# Revit family: AISC WT Shapes-Section
name_source: partatom
category: Detail Items
revit_build: Autodesk Revit Architecture 2012 (Build: 20110210_1515)
units: mm (PartAtom-declared; Revit-internal decimal feet)

## types (275) — shared parameters
Keynote = 05 12 00.N0
y = 0' - 2 31/32"

## per-type parameters (varying)
| type | A | W | bf | d | k | r | tf | tw |
| WT22X167.5 | 0.34 SF | 168 | 1' - 3 29/32" | 1' - 10" | 0' - 2 5/8" | 0' - 0 27/32" | 0' - 1 25/32" | 0' - 1 1/32" |
| WT22X145 | 0.3 SF | 145 | 1' - 3 13/16" | 1' - 9 13/16" | 0' - 2 7/16" | 0' - 0 27/32" | 0' - 1 19/32" | 0' - 0 7/8" |
| WT22X131 | 0.27 SF | 131 | 1' - 3 13/16" | 1' - 9 11/16" | 0' - 2 1/4" | 0' - 0 27/32" | 0' - 1 13/32" | 0' - 0 25/32" |
| WT22X115 | 0.23 SF | 115 | 1' - 3 13/16" | 1' - 9 1/2" | 0' - 2 1/16" | 0' - 0 27/32" | 0' - 1 7/32" | 0' - 0 23/32" |
| WT20X296.5 | 0.61 SF | 296 | 1' - 4 11/16" | 1' - 9 1/2" | 0' - 4 1/2" | 0' - 1 9/32" | 0' - 3 7/32" | 0' - 1 25/32" |
| WT20X251.5 | 0.51 SF | 252 | 1' - 4 13/32" | 1' - 9" | 0' - 4" | 0' - 1 1/4" | 0' - 2 3/4" | 0' - 1 17/32" |
| WT20X215.5 | 0.44 SF | 215 | 1' - 4 3/16" | 1' - 8 19/32" | 0' - 3 5/8" | 0' - 1 1/4" | 0' - 2 3/8" | 0' - 1 11/32" |
| WT20X198.5 | 0.41 SF | 198 | 1' - 4 3/32" | 1' - 8 1/2" | 0' - 3 1/2" | 0' - 1 5/16" | 0' - 2 3/16" | 0' - 1 7/32" |
| WT20X186 | 0.38 SF | 186 | 1' - 4 3/32" | 1' - 8 5/16" | 0' - 3 5/16" | 0' - 1 1/4" | 0' - 2 1/16" | 0' - 1 5/32" |
| WT20X181 | 0.37 SF | 181 | 1' - 4" | 1' - 8 5/16" | 0' - 3 1/4" | 0' - 1 1/4" | 0' - 2" | 0' - 1 1/8" |
| WT20X162 | 0.33 SF | 162 | 1' - 3 29/32" | 1' - 8 3/32" | 0' - 3 1/16" | 0' - 1 1/4" | 0' - 1 13/16" | 0' - 1" |
| WT20X148.5 | 0.3 SF | 148 | 1' - 3 13/16" | 1' - 7 29/32" | 0' - 2 15/16" | 0' - 1 9/32" | 0' - 1 21/32" | 0' - 0 15/16" |
| WT20X138.5 | 0.28 SF | 138 | 1' - 3 13/16" | 1' - 7 13/16" | 0' - 2 7/8" | 0' - 1 9/32" | 0' - 1 19/32" | 0' - 0 27/32" |
| WT20X124.5 | 0.25 SF | 125 | 1' - 3 13/16" | 1' - 7 11/16" | 0' - 2 11/16" | 0' - 1 9/32" | 0' - 1 13/32" | 0' - 0 3/4" |
| WT20X107.5 | 0.22 SF | 108 | 1' - 3 13/16" | 1' - 7 1/2" | 0' - 2 1/2" | 0' - 1 9/32" | 0' - 1 7/32" | 0' - 0 21/32" |
| WT20X99.5 | 0.2 SF | 100 | 1' - 3 13/16" | 1' - 7 5/16" | 0' - 2 5/16" | 0' - 1 1/4" | 0' - 1 1/16" | 0' - 0 21/32" |
| WT20X196 | 0.4 SF | 196 | 1' - 0 13/32" | 1' - 8 13/16" | 0' - 3 13/16" | 0' - 1 9/32" | 0' - 2 17/32" | 0' - 1 13/32" |
| WT20X165.5 | 0.34 SF | 166 | 1' - 0 3/16" | 1' - 8 13/32" | 0' - 3 3/8" | 0' - 1 1/4" | 0' - 2 1/8" | 0' - 1 7/32" |
| WT20X163.5 | 0.33 SF | 164 | 1' - 0 3/32" | 1' - 8 13/32" | 0' - 3 3/8" | 0' - 1 1/4" | 0' - 2 1/8" | 0' - 1 3/16" |
| WT20X147 | 0.3 SF | 147 | 1' - 0" | 1' - 8 3/16" | 0' - 3 3/16" | 0' - 1 1/4" | 0' - 1 15/16" | 0' - 1 1/16" |
| WT20X139 | 0.28 SF | 139 | 1' - 0" | 1' - 8 3/32" | 0' - 3 1/16" | 0' - 1 1/4" | 0' - 1 13/16" | 0' - 1 1/32" |
| WT20X132 | 0.27 SF | 132 | 0' - 11 29/32" | 1' - 8" | 0' - 3" | 0' - 1 9/32" | 0' - 1 23/32" | 0' - 0 31/32" |
| WT20X117.5 | 0.24 SF | 118 | 0' - 11 29/32" | 1' - 7 13/16" | 0' - 2 7/8" | 0' - 1 9/32" | 0' - 1 19/32" | 0' - 0 27/32" |
| WT20X105.5 | 0.22 SF | 106 | 0' - 11 13/16" | 1' - 7 11/16" | 0' - 2 11/16" | 0' - 1 9/32" | 0' - 1 13/32" | 0' - 0 3/4" |
| WT20X91.5 | 0.19 SF | 91.5 | 0' - 11 13/16" | 1' - 7 1/2" | 0' - 2 1/2" | 0' - 1 5/16" | 0' - 1 3/16" | 0' - 0 21/32" |
| WT20X83.5 | 0.17 SF | 83.5 | 0' - 11 13/16" | 1' - 7 5/16" | 0' - 2 5/16" | 0' - 1 9/32" | 0' - 1 1/32" | 0' - 0 21/32" |
| WT20X74.5 | 0.15 SF | 74.5 | 0' - 11 13/16" | 1' - 7 3/32" | 0' - 2 1/8" | 0' - 1 9/32" | 0' - 0 27/32" | 0' - 0 5/8" |
| WT18X400 | 0.82 SF | 400 | 1' - 6" | 1' - 9" | 0' - 5 9/16" | 0' - 1 9/32" | 0' - 4 9/32" | 0' - 2 3/8" |
| WT18X326 | 0.67 SF | 325 | 1' - 5 19/32" | 1' - 8 3/16" | 0' - 4 13/16" | 0' - 1 9/32" | 0' - 3 17/32" | 0' - 1 31/32" |
| WT18X264.5 | 0.54 SF | 264 | 1' - 5 3/16" | 1' - 7 19/32" | 0' - 4 3/16" | 0' - 1 9/32" | 0' - 2 29/32" | 0' - 1 5/8" |
| WT18X243.5 | 0.5 SF | 244 | 1' - 5 3/32" | 1' - 7 11/16" | 0' - 4" | 0' - 1 5/16" | 0' - 2 11/16" | 0' - 1 1/2" |
| WT18X220.5 | 0.45 SF | 220 | 1' - 5" | 1' - 7 3/32" | 0' - 3 11/16" | 0' - 1 1/4" | 0' - 2 7/16" | 0' - 1 3/8" |
| WT18X197.5 | 0.4 SF | 198 | 1' - 4 13/16" | 1' - 6 29/32" | 0' - 3 7/16" | 0' - 1 1/4" | 0' - 2 3/16" | 0' - 1 7/32" |
| WT18X180.5 | 0.37 SF | 180 | 1' - 4 11/16" | 1' - 6 11/16" | 0' - 3 1/4" | 0' - 1 1/4" | 0' - 2" | 0' - 1 1/8" |
| WT18X165 | 0.34 SF | 165 | 1' - 4 19/32" | 1' - 6 1/2" | 0' - 3 1/8" | 0' - 1 9/32" | 0' - 1 27/32" | 0' - 1 1/32" |
| WT18X151 | 0.31 SF | 151 | 1' - 4 11/16" | 1' - 6 13/32" | 0' - 2 15/16" | 0' - 1 1/4" | 0' - 1 11/16" | 0' - 0 15/16" |
| WT18X141 | 0.29 SF | 141 | 1' - 4 19/32" | 1' - 6 5/16" | 0' - 2 13/16" | 0' - 1 1/4" | 0' - 1 9/16" | 0' - 0 7/8" |
| WT18X131 | 0.27 SF | 131 | 1' - 4 19/32" | 1' - 6 3/32" | 0' - 2 11/16" | 0' - 1 1/4" | 0' - 1 7/16" | 0' - 0 27/32" |
| WT18X123.5 | 0.25 SF | 124 | 1' - 4 1/2" | 1' - 6" | 0' - 2 5/8" | 0' - 1 9/32" | 0' - 1 11/32" | 0' - 0 13/16" |
| WT18X116 | 0.24 SF | 116 | 1' - 0 3/32" | 1' - 6 19/32" | 0' - 2 7/16" | 0' - 0 7/8" | 0' - 1 9/16" | 0' - 0 7/8" |
| WT18X128 | 0.26 SF | 128 | 1' - 0 3/16" | 1' - 6 11/16" | 0' - 2 5/8" | 0' - 0 29/32" | 0' - 1 23/32" | 0' - 0 31/32" |
| WT18X115.5 | 0.24 SF | 116 | 1' - 0 3/32" | 1' - 6 19/32" | 0' - 2 7/16" | 0' - 0 7/8" | 0' - 1 9/16" | 0' - 0 7/8" |
| WT18X105 | 0.21 SF | 105 | 1' - 0 3/16" | 1' - 6 5/16" | 0' - 2 5/16" | 0' - 0 15/16" | 0' - 1 3/8" | 0' - 0 27/32" |
| WT18X97 | 0.2 SF | 97 | 1' - 0 3/32" | 1' - 6 3/16" | 0' - 2 3/16" | 0' - 0 15/16" | 0' - 1 1/4" | 0' - 0 3/4" |
| WT18X91 | 0.19 SF | 91 | 1' - 0 3/32" | 1' - 6 3/16" | 0' - 2 1/8" | 0' - 0 15/16" | 0' - 1 3/16" | 0' - 0 23/32" |
| WT18X85 | 0.17 SF | 85 | 1' - 0" | 1' - 6 3/32" | 0' - 2" | 0' - 0 29/32" | 0' - 1 3/32" | 0' - 0 11/16" |
| WT18X80 | 0.16 SF | 80 | 1' - 0" | 1' - 6" | 0' - 1 15/16" | 0' - 0 29/32" | 0' - 1 1/32" | 0' - 0 21/32" |
| WT18X75 | 0.15 SF | 75 | 1' - 0" | 1' - 5 29/32" | 0' - 1 7/8" | 0' - 0 15/16" | 0' - 0 15/16" | 0' - 0 5/8" |
| WT18X67.5 | 0.14 SF | 67.5 | 1' - 0" | 1' - 5 13/16" | 0' - 1 11/16" | 0' - 0 29/32" | 0' - 0 25/32" | 0' - 0 19/32" |
| WT16.5X193.5 | 0.4 SF | 194 | 1' - 4 3/16" | 1' - 6" | 0' - 3 3/16" | 0' - 0 29/32" | 0' - 2 9/32" | 0' - 1 1/4" |
| WT16.5X177 | 0.36 SF | 177 | 1' - 4 3/32" | 1' - 5 13/16" | 0' - 2 15/16" | 0' - 0 27/32" | 0' - 2 3/32" | 0' - 1 5/32" |
| WT16.5X159 | 0.33 SF | 159 | 1' - 4" | 1' - 5 19/32" | 0' - 2 3/4" | 0' - 0 7/8" | 0' - 1 7/8" | 0' - 1 1/32" |
| WT16.5X145.5 | 0.3 SF | 146 | 1' - 3 29/32" | 1' - 5 13/32" | 0' - 2 5/8" | 0' - 0 29/32" | 0' - 1 23/32" | 0' - 0 31/32" |
| WT16.5X131.5 | 0.27 SF | 132 | 1' - 3 13/16" | 1' - 5 5/16" | 0' - 2 7/16" | 0' - 0 7/8" | 0' - 1 9/16" | 0' - 0 7/8" |
| WT16.5X120.5 | 0.25 SF | 120 | 1' - 3 29/32" | 1' - 5 3/32" | 0' - 2 1/4" | 0' - 0 27/32" | 0' - 1 13/32" | 0' - 0 27/32" |
| WT16.5X110.5 | 0.23 SF | 110 | 1' - 3 13/16" | 1' - 5" | 0' - 2 1/8" | 0' - 0 27/32" | 0' - 1 9/32" | 0' - 0 25/32" |
| WT16.5X100.5 | 0.21 SF | 100 | 1' - 3 11/16" | 1' - 4 13/16" | 0' - 2" | 0' - 0 27/32" | 0' - 1 5/32" | 0' - 0 23/32" |
| WT16.5X84.5 | 0.17 SF | 84.5 | 0' - 11 1/2" | 1' - 4 29/32" | 0' - 2 1/8" | 0' - 0 29/32" | 0' - 1 7/32" | 0' - 0 21/32" |
| WT16.5X76 | 0.16 SF | 76 | 0' - 11 19/32" | 1' - 4 11/16" | 0' - 1 15/16" | 0' - 0 7/8" | 0' - 1 1/16" | 0' - 0 5/8" |
| WT16.5X70.5 | 0.14 SF | 70.5 | 0' - 11 1/2" | 1' - 4 11/16" | 0' - 1 13/16" | 0' - 0 27/32" | 0' - 0 31/32" | 0' - 0 19/32" |
| WT16.5X65 | 0.13 SF | 65 | 0' - 11 1/2" | 1' - 4 1/2" | 0' - 1 3/4" | 0' - 0 29/32" | 0' - 0 27/32" | 0' - 0 19/32" |
| WT16.5X59 | 0.12 SF | 59 | 0' - 11 1/2" | 1' - 4 13/32" | 0' - 1 5/8" | 0' - 0 7/8" | 0' - 0 3/4" | 0' - 0 9/16" |
| WT15X195.5 | 0.4 SF | 196 | 1' - 3 19/32" | 1' - 4 19/32" | 0' - 3 3/8" | 0' - 0 15/16" | 0' - 2 7/16" | 0' - 1 3/8" |
| WT15X178.5 | 0.36 SF | 178 | 1' - 3 1/2" | 1' - 4 13/32" | 0' - 3 1/8" | 0' - 0 7/8" | 0' - 2 1/4" | 0' - 1 1/4" |
| WT15X163 | 0.33 SF | 163 | 1' - 3 13/32" | 1' - 4 3/16" | 0' - 2 15/16" | 0' - 0 7/8" | 0' - 2 1/16" | 0' - 1 1/8" |
| WT15X146 | 0.3 SF | 146 | 1' - 3 5/16" | 1' - 4" | 0' - 2 3/4" | 0' - 0 29/32" | 0' - 1 27/32" | 0' - 1 1/32" |
| WT15X130.5 | 0.27 SF | 130 | 1' - 3 3/16" | 1' - 3 13/16" | 0' - 2 9/16" | 0' - 0 29/32" | 0' - 1 21/32" | 0' - 0 15/16" |
| WT15X117.5 | 0.24 SF | 118 | 1' - 3 3/32" | 1' - 3 11/16" | 0' - 2 3/8" | 0' - 0 7/8" | 0' - 1 1/2" | 0' - 0 27/32" |
| WT15X105.5 | 0.22 SF | 106 | 1' - 3 3/32" | 1' - 3 1/2" | 0' - 2 1/4" | 0' - 0 15/16" | 0' - 1 5/16" | 0' - 0 25/32" |
| WT15X95.5 | 0.2 SF | 95.5 | 1' - 3" | 1' - 3 5/16" | 0' - 2 1/16" | 0' - 0 7/8" | 0' - 1 3/16" | 0' - 0 23/32" |
| WT15X86.5 | 0.18 SF | 86.5 | 1' - 3" | 1' - 3 3/16" | 0' - 2" | 0' - 0 15/16" | 0' - 1 1/16" | 0' - 0 21/32" |
| WT15X74 | 0.15 SF | 74 | 0' - 10 1/2" | 1' - 3 5/16" | 0' - 2 1/16" | 0' - 0 7/8" | 0' - 1 3/16" | 0' - 0 21/32" |
| WT15X66 | 0.13 SF | 66 | 0' - 10 1/2" | 1' - 3 3/16" | 0' - 1 7/8" | 0' - 0 7/8" | 0' - 1" | 0' - 0 5/8" |
| WT15X62 | 0.13 SF | 62 | 0' - 10 1/2" | 1' - 3 3/32" | 0' - 1 13/16" | 0' - 0 7/8" | 0' - 0 15/16" | 0' - 0 19/32" |
| WT15X58 | 0.12 SF | 58 | 0' - 10 1/2" | 1' - 3" | 0' - 1 3/4" | 0' - 0 29/32" | 0' - 0 27/32" | 0' - 0 9/16" |
| WT15X54 | 0.11 SF | 54 | 0' - 10 1/2" | 1' - 2 29/32" | 0' - 1 11/16" | 0' - 0 15/16" | 0' - 0 3/4" | 0' - 0 17/32" |
| WT15X49.5 | 0.1 SF | 49.5 | 0' - 10 1/2" | 1' - 2 13/16" | 0' - 1 9/16" | 0' - 0 29/32" | 0' - 0 21/32" | 0' - 0 17/32" |
| WT15X45 | 0.09 SF | 45 | 0' - 10 13/32" | 1' - 2 13/16" | 0' - 1 1/2" | 0' - 0 7/8" | 0' - 0 5/8" | 0' - 0 15/32" |
| WT13.5X269.5 | 0.55 SF | 270 | 1' - 3 5/16" | 1' - 4 5/16" | 0' - 4 7/16" | 0' - 0 29/32" | 0' - 3 17/32" | 0' - 1 31/32" |
| WT13.5X184 | 0.38 SF | 184 | 1' - 2 11/16" | 1' - 3 3/16" | 0' - 3 3/8" | 0' - 0 29/32" | 0' - 2 15/32" | 0' - 1 3/8" |
| WT13.5X168 | 0.34 SF | 168 | 1' - 2 19/32" | 1' - 3" | 0' - 3 3/16" | 0' - 0 29/32" | 0' - 2 9/32" | 0' - 1 1/4" |
| WT13.5X153.5 | 0.31 SF | 154 | 1' - 2 13/32" | 1' - 2 13/16" | 0' - 3" | 0' - 0 29/32" | 0' - 2 3/32" | 0' - 1 5/32" |
| WT13.5X140.5 | 0.29 SF | 140 | 1' - 2 13/32" | 1' - 2 19/32" | 0' - 2 13/16" | 0' - 0 7/8" | 0' - 1 15/16" | 0' - 1 1/16" |
| WT13.5X129 | 0.26 SF | 129 | 1' - 2 5/16" | 1' - 2 1/2" | 0' - 2 11/16" | 0' - 0 29/32" | 0' - 1 25/32" | 0' - 0 31/32" |
| WT13.5X117.5 | 0.24 SF | 118 | 1' - 2 3/16" | 1' - 2 5/16" | 0' - 2 1/2" | 0' - 0 7/8" | 0' - 1 5/8" | 0' - 0 29/32" |
| WT13.5X108.5 | 0.22 SF | 108 | 1' - 2 3/32" | 1' - 2 3/16" | 0' - 2 3/8" | 0' - 0 7/8" | 0' - 1 1/2" | 0' - 0 27/32" |
| WT13.5X97 | 0.2 SF | 97 | 1' - 2" | 1' - 2 3/32" | 0' - 2 1/4" | 0' - 0 29/32" | 0' - 1 11/32" | 0' - 0 3/4" |
| WT13.5X89 | 0.18 SF | 89 | 1' - 2 3/32" | 1' - 1 29/32" | 0' - 2 1/16" | 0' - 0 7/8" | 0' - 1 3/16" | 0' - 0 23/32" |
| WT13.5X80.5 | 0.17 SF | 80.5 | 1' - 2" | 1' - 1 13/16" | 0' - 2" | 0' - 0 29/32" | 0' - 1 3/32" | 0' - 0 21/32" |
| WT13.5X73 | 0.15 SF | 73 | 1' - 2" | 1' - 1 11/16" | 0' - 1 7/8" | 0' - 0 29/32" | 0' - 0 31/32" | 0' - 0 19/32" |
| WT13.5X64.5 | 0.13 SF | 64.5 | 0' - 10" | 1' - 1 13/16" | 0' - 2" | 0' - 0 29/32" | 0' - 1 3/32" | 0' - 0 5/8" |
| WT13.5X57 | 0.12 SF | 57 | 0' - 10 3/32" | 1' - 1 19/32" | 0' - 1 13/16" | 0' - 0 7/8" | 0' - 0 15/16" | 0' - 0 9/16" |
| WT13.5X51 | 0.1 SF | 51 | 0' - 10" | 1' - 1 1/2" | 0' - 1 3/4" | 0' - 0 29/32" | 0' - 0 27/32" | 0' - 0 1/2" |
| WT13.5X47 | 0.1 SF | 47 | 0' - 10" | 1' - 1 1/2" | 0' - 1 5/8" | 0' - 0 7/8" | 0' - 0 3/4" | 0' - 0 1/2" |
| WT13.5X42 | 0.09 SF | 42 | 0' - 10" | 1' - 1 13/32" | 0' - 1 9/16" | 0' - 0 15/16" | 0' - 0 5/8" | 0' - 0 15/32" |
| WT12X185 | 0.38 SF | 185 | 1' - 1 11/16" | 1' - 2" | 0' - 3 5/8" | 0' - 0 29/32" | 0' - 2 23/32" | 0' - 1 17/32" |
| WT12X167.5 | 0.34 SF | 168 | 1' - 1 1/2" | 1' - 1 13/16" | 0' - 3 3/8" | 0' - 0 29/32" | 0' - 2 15/32" | 0' - 1 3/8" |
| WT12X153 | 0.31 SF | 153 | 1' - 1 13/32" | 1' - 1 19/32" | 0' - 3 3/16" | 0' - 0 29/32" | 0' - 2 9/32" | 0' - 1 1/4" |
| WT12X139.5 | 0.28 SF | 140 | 1' - 1 5/16" | 1' - 1 13/32" | 0' - 3" | 0' - 0 29/32" | 0' - 2 3/32" | 0' - 1 5/32" |
| WT12X125 | 0.26 SF | 125 | 1' - 1 3/16" | 1' - 1 3/16" | 0' - 2 13/16" | 0' - 0 15/16" | 0' - 1 7/8" | 0' - 1 1/32" |
| WT12X114.5 | 0.23 SF | 114 | 1' - 1 3/32" | 1' - 1" | 0' - 2 5/8" | 0' - 0 29/32" | 0' - 1 23/32" | 0' - 0 31/32" |
| WT12X103.5 | 0.21 SF | 103 | 1' - 1" | 1' - 0 29/32" | 0' - 2 1/2" | 0' - 0 15/16" | 0' - 1 9/16" | 0' - 0 7/8" |
| WT12X96 | 0.2 SF | 96 | 1' - 1" | 1' - 0 11/16" | 0' - 2 3/8" | 0' - 0 29/32" | 0' - 1 15/32" | 0' - 0 13/16" |
| WT12X88 | 0.18 SF | 88 | 1' - 0 29/32" | 1' - 0 19/32" | 0' - 2 1/4" | 0' - 0 29/32" | 0' - 1 11/32" | 0' - 0 3/4" |
| WT12X81 | 0.17 SF | 81 | 1' - 1" | 1' - 0 1/2" | 0' - 2 1/8" | 0' - 0 29/32" | 0' - 1 7/32" | 0' - 0 23/32" |
| WT12X73 | 0.15 SF | 73 | 1' - 0 29/32" | 1' - 0 13/32" | 0' - 2" | 0' - 0 29/32" | 0' - 1 3/32" | 0' - 0 21/32" |
| WT12X65.5 | 0.13 SF | 65.5 | 1' - 0 29/32" | 1' - 0 3/16" | 0' - 1 7/8" | 0' - 0 29/32" | 0' - 0 31/32" | 0' - 0 19/32" |
| WT12X58.5 | 0.12 SF | 58.5 | 1' - 0 13/16" | 1' - 0 3/32" | 0' - 1 3/4" | 0' - 0 29/32" | 0' - 0 27/32" | 0' - 0 9/16" |
| WT12X52 | 0.11 SF | 52 | 1' - 0 13/16" | 1' - 0" | 0' - 1 5/8" | 0' - 0 7/8" | 0' - 0 3/4" | 0' - 0 1/2" |
| WT12X51.5 | 0.1 SF | 51.5 | 0' - 9" | 1' - 0 5/16" | 0' - 1 7/8" | 0' - 0 29/32" | 0' - 0 31/32" | 0' - 0 9/16" |
| WT12X47 | 0.1 SF | 47 | 0' - 9 1/16" | 1' - 0 3/16" | 0' - 1 3/4" | 0' - 0 7/8" | 0' - 0 7/8" | 0' - 0 1/2" |
| WT12X42 | 0.09 SF | 42 | 0' - 9 1/32" | 1' - 0 3/32" | 0' - 1 11/16" | 0' - 0 29/32" | 0' - 0 25/32" | 0' - 0 15/32" |
| WT12X38 | 0.08 SF | 38 | 0' - 9" | 1' - 0" | 0' - 1 9/16" | 0' - 0 7/8" | 0' - 0 11/16" | 0' - 0 7/16" |
| WT12X34 | 0.07 SF | 34 | 0' - 8 31/32" | 0' - 11 29/32" | 0' - 1 1/2" | 0' - 0 29/32" | 0' - 0 19/32" | 0' - 0 13/32" |
| WT12X31 | 0.06 SF | 31 | 0' - 7 1/32" | 0' - 11 29/32" | 0' - 1 1/2" | 0' - 0 29/32" | 0' - 0 19/32" | 0' - 0 7/16" |
| WT12X27.5 | 0.06 SF | 27.5 | 0' - 7" | 0' - 11 13/16" | 0' - 1 7/16" | 0' - 0 15/16" | 0' - 0 1/2" | 0' - 0 13/32" |
| WT10.5X100.5 | 0.21 SF | 100 | 1' - 0 19/32" | 0' - 11 1/2" | 0' - 2 1/2" | 0' - 0 7/8" | 0' - 1 5/8" | 0' - 0 29/32" |
| WT10.5X91 | 0.19 SF | 91 | 1' - 0 1/2" | 0' - 11 13/32" | 0' - 2 3/8" | 0' - 0 29/32" | 0' - 1 15/32" | 0' - 0 27/32" |
| WT10.5X83 | 0.17 SF | 83 | 1' - 0 13/32" | 0' - 11 3/16" | 0' - 2 1/4" | 0' - 0 7/8" | 0' - 1 3/8" | 0' - 0 3/4" |
| WT10.5X73.5 | 0.15 SF | 73.5 | 1' - 0 1/2" | 0' - 11" | 0' - 2" | 0' - 0 27/32" | 0' - 1 5/32" | 0' - 0 23/32" |
| WT10.5X66 | 0.13 SF | 66 | 1' - 0 13/32" | 0' - 10 29/32" | 0' - 1 15/16" | 0' - 0 29/32" | 0' - 1 1/32" | 0' - 0 21/32" |
| WT10.5X61 | 0.12 SF | 61 | 1' - 0 13/32" | 0' - 10 13/16" | 0' - 1 13/16" | 0' - 0 27/32" | 0' - 0 31/32" | 0' - 0 19/32" |
| WT10.5X55.5 | 0.11 SF | 55.5 | 1' - 0 5/16" | 0' - 10 13/16" | 0' - 1 3/4" | 0' - 0 7/8" | 0' - 0 7/8" | 0' - 0 9/16" |
| WT10.5X50.5 | 0.1 SF | 50.5 | 1' - 0 5/16" | 0' - 10 11/16" | 0' - 1 11/16" | 0' - 0 7/8" | 0' - 0 13/16" | 0' - 0 1/2" |
| WT10.5X46.5 | 0.1 SF | 46.5 | 0' - 8 13/32" | 0' - 10 13/16" | 0' - 1 5/8" | 0' - 0 11/16" | 0' - 0 15/16" | 0' - 0 19/32" |
| WT10.5X41.5 | 0.08 SF | 41.5 | 0' - 8 3/8" | 0' - 10 11/16" | 0' - 1 1/2" | 0' - 0 21/32" | 0' - 0 27/32" | 0' - 0 1/2" |
| WT10.5X36.5 | 0.07 SF | 36.5 | 0' - 8 5/16" | 0' - 10 19/32" | 0' - 1 7/16" | 0' - 0 11/16" | 0' - 0 3/4" | 0' - 0 15/32" |
| WT10.5X34 | 0.07 SF | 34 | 0' - 8 9/32" | 0' - 10 19/32" | 0' - 1 3/8" | 0' - 0 11/16" | 0' - 0 11/16" | 0' - 0 7/16" |
| WT10.5X31 | 0.06 SF | 31 | 0' - 8 1/4" | 0' - 10 1/2" | 0' - 1 5/16" | 0' - 0 11/16" | 0' - 0 5/8" | 0' - 0 13/32" |
| WT10.5X27.5 | 0.06 SF | 27.5 | 0' - 8 7/32" | 0' - 10 13/32" | 0' - 1 3/16" | 0' - 0 21/32" | 0' - 0 17/32" | 0' - 0 3/8" |
| WT10.5X24 | 0.05 SF | 24 | 0' - 8 1/8" | 0' - 10 5/16" | 0' - 1 1/8" | 0' - 0 11/16" | 0' - 0 7/16" | 0' - 0 11/32" |
| WT10.5X28.5 | 0.06 SF | 28.5 | 0' - 6 9/16" | 0' - 10 1/2" | 0' - 1 5/16" | 0' - 0 21/32" | 0' - 0 21/32" | 0' - 0 13/32" |
| WT10.5X25 | 0.05 SF | 25 | 0' - 6 17/32" | 0' - 10 13/32" | 0' - 1 1/4" | 0' - 0 23/32" | 0' - 0 17/32" | 0' - 0 3/8" |
| WT10.5X22 | 0.05 SF | 22 | 0' - 6 1/2" | 0' - 10 5/16" | 0' - 1 1/8" | 0' - 0 11/16" | 0' - 0 7/16" | 0' - 0 11/32" |
| WT9X155.5 | 0.32 SF | 156 | 1' - 0" | 0' - 11 3/16" | 0' - 3 7/16" | 0' - 0 11/16" | 0' - 2 3/4" | 0' - 1 17/32" |
| WT9X141.5 | 0.29 SF | 142 | 0' - 11 29/32" | 0' - 10 29/32" | 0' - 3 3/16" | 0' - 0 11/16" | 0' - 2 1/2" | 0' - 1 13/32" |
| WT9X129 | 0.26 SF | 129 | 0' - 11 13/16" | 0' - 10 11/16" | 0' - 3" | 0' - 0 11/16" | 0' - 2 5/16" | 0' - 1 9/32" |
| WT9X117 | 0.24 SF | 117 | 0' - 11 11/16" | 0' - 10 1/2" | 0' - 2 3/4" | 0' - 0 5/8" | 0' - 2 1/8" | 0' - 1 5/32" |
| WT9X105.5 | 0.22 SF | 106 | 0' - 11 19/32" | 0' - 10 5/16" | 0' - 2 9/16" | 0' - 0 21/32" | 0' - 1 29/32" | 0' - 1 1/16" |
| WT9X96 | 0.2 SF | 97 | 0' - 11 1/2" | 0' - 10 3/16" | 0' - 2 7/16" | 0' - 0 11/16" | 0' - 1 3/4" | 0' - 0 31/32" |
| WT9X87.5 | 0.18 SF | 87.5 | 0' - 11 13/32" | 0' - 10" | 0' - 2 7/16" | 0' - 0 27/32" | 0' - 1 19/32" | 0' - 0 7/8" |
| WT9X79 | 0.16 SF | 79 | 0' - 11 5/16" | 0' - 9 7/8" | 0' - 2 3/8" | 0' - 0 15/16" | 0' - 1 7/16" | 0' - 0 13/16" |
| WT9X71.5 | 0.15 SF | 71.5 | 0' - 11 3/16" | 0' - 9 3/4" | 0' - 2 3/16" | 0' - 0 7/8" | 0' - 1 5/16" | 0' - 0 23/32" |
| WT9X65 | 0.13 SF | 65 | 0' - 11 3/16" | 0' - 9 5/8" | 0' - 2 1/16" | 0' - 0 7/8" | 0' - 1 3/16" | 0' - 0 21/32" |
| WT9X59.5 | 0.12 SF | 59.5 | 0' - 11 5/16" | 0' - 9 1/2" | 0' - 1 15/16" | 0' - 0 7/8" | 0' - 1 1/16" | 0' - 0 21/32" |
| WT9X53 | 0.11 SF | 53 | 0' - 11 3/16" | 0' - 9 3/8" | 0' - 1 13/16" | 0' - 0 7/8" | 0' - 0 15/16" | 0' - 0 19/32" |
| WT9X48.5 | 0.1 SF | 48.5 | 0' - 11 3/32" | 0' - 9 5/16" | 0' - 1 3/4" | 0' - 0 7/8" | 0' - 0 7/8" | 0' - 0 17/32" |
| WT9X43 | 0.09 SF | 43 | 0' - 11 3/32" | 0' - 9 3/16" | 0' - 1 5/8" | 0' - 0 27/32" | 0' - 0 25/32" | 0' - 0 15/32" |
| WT9X38 | 0.08 SF | 38 | 0' - 11" | 0' - 9 1/8" | 0' - 1 9/16" | 0' - 0 7/8" | 0' - 0 11/16" | 0' - 0 7/16" |
| WT9X35.5 | 0.07 SF | 35.5 | 0' - 7 5/8" | 0' - 9 1/4" | 0' - 1 1/2" | 0' - 0 11/16" | 0' - 0 13/16" | 0' - 0 1/2" |
| WT9X32.5 | 0.07 SF | 32.5 | 0' - 7 19/32" | 0' - 9 3/16" | 0' - 1 7/16" | 0' - 0 11/16" | 0' - 0 3/4" | 0' - 0 7/16" |
| WT9X30 | 0.06 SF | 30 | 0' - 7 9/16" | 0' - 9 1/8" | 0' - 1 3/8" | 0' - 0 11/16" | 0' - 0 11/16" | 0' - 0 13/32" |
| WT9X27.5 | 0.06 SF | 27.5 | 0' - 7 17/32" | 0' - 9 1/16" | 0' - 1 5/16" | 0' - 0 11/16" | 0' - 0 5/8" | 0' - 0 3/8" |
| WT9X25 | 0.05 SF | 25 | 0' - 7 1/2" | 0' - 9" | 0' - 1 1/4" | 0' - 0 11/16" | 0' - 0 9/16" | 0' - 0 11/32" |
| WT9X23 | 0.05 SF | 23 | 0' - 6 1/16" | 0' - 9 1/32" | 0' - 1 1/4" | 0' - 0 21/32" | 0' - 0 19/32" | 0' - 0 3/8" |
| WT9X20 | 0.04 SF | 20 | 0' - 6 1/32" | 0' - 8 15/16" | 0' - 1 3/16" | 0' - 0 21/32" | 0' - 0 17/32" | 0' - 0 5/16" |
| WT9X17.5 | 0.04 SF | 17.5 | 0' - 6" | 0' - 8 27/32" | 0' - 1 1/8" | 0' - 0 11/16" | 0' - 0 7/16" | 0' - 0 5/16" |
| WT8X50 | 0.1 SF | 50 | 0' - 10 13/32" | 0' - 8 1/2" | 0' - 1 7/8" | 0' - 0 7/8" | 0' - 1" | 0' - 0 19/32" |
| WT8X44.5 | 0.09 SF | 44.5 | 0' - 10 13/32" | 0' - 8 3/8" | 0' - 1 3/4" | 0' - 0 7/8" | 0' - 0 7/8" | 0' - 0 17/32" |
| WT8X38.5 | 0.08 SF | 38.5 | 0' - 10 5/16" | 0' - 8 1/4" | 0' - 1 5/8" | 0' - 0 7/8" | 0' - 0 3/4" | 0' - 0 15/32" |
| WT8X33.5 | 0.07 SF | 33.5 | 0' - 10 3/16" | 0' - 8 5/32" | 0' - 1 9/16" | 0' - 0 29/32" | 0' - 0 21/32" | 0' - 0 13/32" |
| WT8X28.5 | 0.06 SF | 28.5 | 0' - 7 1/8" | 0' - 8 7/32" | 0' - 1 3/8" | 0' - 0 21/32" | 0' - 0 23/32" | 0' - 0 7/16" |
| WT8X25 | 0.05 SF | 25 | 0' - 7 1/16" | 0' - 8 1/8" | 0' - 1 5/16" | 0' - 0 11/16" | 0' - 0 5/8" | 0' - 0 3/8" |
| WT8X22.5 | 0.05 SF | 22.5 | 0' - 7 1/32" | 0' - 8 1/16" | 0' - 1 1/4" | 0' - 0 11/16" | 0' - 0 9/16" | 0' - 0 11/32" |
| WT8X20 | 0.04 SF | 20 | 0' - 7" | 0' - 8" | 0' - 1 3/16" | 0' - 0 11/16" | 0' - 0 1/2" | 0' - 0 5/16" |
| WT8X18 | 0.04 SF | 18 | 0' - 7" | 0' - 7 15/16" | 0' - 1 1/8" | 0' - 0 11/16" | 0' - 0 7/16" | 0' - 0 9/32" |
| WT8X15.5 | 0.03 SF | 15.5 | 0' - 5 17/32" | 0' - 7 15/16" | 0' - 1 1/8" | 0' - 0 11/16" | 0' - 0 7/16" | 0' - 0 9/32" |
| WT8X13 | 0.03 SF | 13 | 0' - 5 1/2" | 0' - 7 27/32" | 0' - 1 1/16" | 0' - 0 23/32" | 0' - 0 11/32" | 0' - 0 1/4" |
| WT7X404 - Obsolete | 0.83 SF | 404 | 1' - 6 19/32" | 0' - 11 13/32" | 0' - 6 7/16" | 0' - 1 5/16" | 0' - 5 1/8" | 0' - 3 3/4" |
| WT7X365 | 0.74 SF | 365 | 1' - 5 29/32" | 0' - 11 3/16" | 0' - 6 3/16" | 0' - 1 9/32" | 0' - 4 29/32" | 0' - 3 1/16" |
| WT7X332.5 | 0.68 SF | 332 | 1' - 5 11/16" | 0' - 10 13/16" | 0' - 5 13/16" | 0' - 1 9/32" | 0' - 4 17/32" | 0' - 2 27/32" |
| WT7X302.5 | 0.62 SF | 302 | 1' - 5 13/32" | 0' - 10 1/2" | 0' - 5 7/16" | 0' - 1 9/32" | 0' - 4 5/32" | 0' - 2 19/32" |
| WT7X275 | 0.56 SF | 275 | 1' - 5 3/16" | 0' - 10 3/32" | 0' - 5 1/8" | 0' - 1 5/16" | 0' - 3 13/16" | 0' - 2 3/8" |
| WT7X250 | 0.51 SF | 250 | 1' - 5" | 0' - 9 13/16" | 0' - 4 13/16" | 0' - 1 5/16" | 0' - 3 1/2" | 0' - 2 3/16" |
| WT7X227.5 | 0.46 SF | 228 | 1' - 4 13/16" | 0' - 9 1/2" | 0' - 4 1/2" | 0' - 1 9/32" | 0' - 3 7/32" | 0' - 2 1/32" |
| WT7X213 | 0.43 SF | 213 | 1' - 4 11/16" | 0' - 9 11/32" | 0' - 4 5/16" | 0' - 1 9/32" | 0' - 3 1/32" | 0' - 1 7/8" |
| WT7X199 | 0.41 SF | 199 | 1' - 4 19/32" | 0' - 9 5/32" | 0' - 4 1/8" | 0' - 1 9/32" | 0' - 2 27/32" | 0' - 1 25/32" |
| WT7X185 | 0.38 SF | 185 | 1' - 4 1/2" | 0' - 8 31/32" | 0' - 3 15/16" | 0' - 1 9/32" | 0' - 2 21/32" | 0' - 1 21/32" |
| WT7X171 | 0.35 SF | 171 | 1' - 4 13/32" | 0' - 8 25/32" | 0' - 3 3/4" | 0' - 1 9/32" | 0' - 2 15/32" | 0' - 1 17/32" |
| WT7X155.5 | 0.32 SF | 156 | 1' - 4 3/16" | 0' - 8 9/16" | 0' - 3 9/16" | 0' - 1 5/16" | 0' - 2 1/4" | 0' - 1 13/32" |
| WT7X141.5 | 0.29 SF | 142 | 1' - 4 3/32" | 0' - 8 3/8" | 0' - 3 3/8" | 0' - 1 5/16" | 0' - 2 1/16" | 0' - 1 9/32" |
| WT7X128.5 | 0.26 SF | 128 | 1' - 4" | 0' - 8 3/16" | 0' - 3 3/16" | 0' - 1 5/16" | 0' - 1 7/8" | 0' - 1 3/16" |
| WT7X116.5 | 0.24 SF | 116 | 1' - 3 29/32" | 0' - 8 1/32" | 0' - 3" | 0' - 1 9/32" | 0' - 1 23/32" | 0' - 1 1/16" |
| WT7X105.5 | 0.22 SF | 106 | 1' - 3 13/16" | 0' - 7 7/8" | 0' - 2 7/8" | 0' - 1 5/16" | 0' - 1 9/16" | 0' - 0 31/32" |
| WT7X96.5 | 0.2 SF | 96.5 | 1' - 3 11/16" | 0' - 7 3/4" | 0' - 2 3/4" | 0' - 1 5/16" | 0' - 1 7/16" | 0' - 0 7/8" |
| WT7X88 | 0.18 SF | 88 | 1' - 3 11/16" | 0' - 7 5/8" | 0' - 2 5/8" | 0' - 1 5/16" | 0' - 1 5/16" | 0' - 0 27/32" |
| WT7X79.5 | 0.16 SF | 79.5 | 1' - 3 19/32" | 0' - 7 1/2" | 0' - 2 1/2" | 0' - 1 5/16" | 0' - 1 3/16" | 0' - 0 3/4" |
| WT7X72.5 | 0.15 SF | 72.5 | 1' - 3 1/2" | 0' - 7 3/8" | 0' - 2 3/8" | 0' - 1 9/32" | 0' - 1 3/32" | 0' - 0 11/16" |
| WT7X66 | 0.13 SF | 66 | 1' - 2 11/16" | 0' - 7 11/32" | 0' - 2 5/16" | 0' - 1 9/32" | 0' - 1 1/32" | 0' - 0 21/32" |
| WT7X60 | 0.12 SF | 60 | 1' - 2 11/16" | 0' - 7 1/4" | 0' - 2 1/4" | 0' - 1 5/16" | 0' - 0 15/16" | 0' - 0 19/32" |
| WT7X54.5 | 0.11 SF | 54.5 | 1' - 2 19/32" | 0' - 7 5/32" | 0' - 2 3/16" | 0' - 1 5/16" | 0' - 0 7/8" | 0' - 0 17/32" |
| WT7X49.5 | 0.1 SF | 49.5 | 1' - 2 19/32" | 0' - 7 3/32" | 0' - 2 1/16" | 0' - 1 9/32" | 0' - 0 25/32" | 0' - 0 1/2" |
| WT7X45 | 0.09 SF | 45 | 1' - 2 1/2" | 0' - 7" | 0' - 2" | 0' - 1 9/32" | 0' - 0 23/32" | 0' - 0 7/16" |
| WT7X41 | 0.08 SF | 41 | 0' - 10 3/32" | 0' - 7 5/32" | 0' - 1 11/16" | 0' - 0 27/32" | 0' - 0 27/32" | 0' - 0 1/2" |
| WT7X37 | 0.08 SF | 37 | 0' - 10 3/32" | 0' - 7 3/32" | 0' - 1 5/8" | 0' - 0 27/32" | 0' - 0 25/32" | 0' - 0 7/16" |
| WT7X34 | 0.07 SF | 34 | 0' - 10" | 0' - 7 1/32" | 0' - 1 9/16" | 0' - 0 27/32" | 0' - 0 23/32" | 0' - 0 13/32" |
| WT7X30.5 | 0.06 SF | 30.5 | 0' - 10" | 0' - 6 15/16" | 0' - 1 1/2" | 0' - 0 27/32" | 0' - 0 21/32" | 0' - 0 3/8" |
| WT7X26.5 | 0.05 SF | 26.5 | 0' - 8 1/16" | 0' - 6 31/32" | 0' - 1 1/2" | 0' - 0 27/32" | 0' - 0 21/32" | 0' - 0 3/8" |
| WT7X24 | 0.05 SF | 24 | 0' - 8 1/32" | 0' - 6 29/32" | 0' - 1 7/16" | 0' - 0 27/32" | 0' - 0 19/32" | 0' - 0 11/32" |
| WT7X21.5 | 0.04 SF | 21.5 | 0' - 8" | 0' - 6 27/32" | 0' - 1 3/8" | 0' - 0 27/32" | 0' - 0 17/32" | 0' - 0 5/16" |
| WT7X19 | 0.04 SF | 19 | 0' - 6 25/32" | 0' - 7 1/16" | 0' - 1 1/4" | 0' - 0 3/4" | 0' - 0 1/2" | 0' - 0 5/16" |
| WT7X17 | 0.03 SF | 17 | 0' - 6 3/4" | 0' - 7" | 0' - 1 3/16" | 0' - 0 23/32" | 0' - 0 15/32" | 0' - 0 9/32" |
| WT7X15 | 0.03 SF | 15 | 0' - 6 23/32" | 0' - 6 29/32" | 0' - 1 1/8" | 0' - 0 3/4" | 0' - 0 3/8" | 0' - 0 9/32" |
| WT7X13 | 0.03 SF | 13 | 0' - 5 1/32" | 0' - 6 31/32" | 0' - 1 1/8" | 0' - 0 23/32" | 0' - 0 13/32" | 0' - 0 1/4" |
| WT7X11 | 0.02 SF | 11 | 0' - 5" | 0' - 6 7/8" | 0' - 1 1/16" | 0' - 0 23/32" | 0' - 0 11/32" | 0' - 0 7/32" |
| WT6X168 | 0.34 SF | 168 | 1' - 1 13/32" | 0' - 8 13/32" | 0' - 3 7/8" | 0' - 0 29/32" | 0' - 2 31/32" | 0' - 1 25/32" |
| WT6X152.5 | 0.31 SF | 152 | 1' - 1 3/16" | 0' - 8 5/32" | 0' - 3 5/8" | 0' - 0 29/32" | 0' - 2 23/32" | 0' - 1 5/8" |
| WT6X139.5 | 0.28 SF | 140 | 1' - 1 3/32" | 0' - 7 15/16" | 0' - 3 3/8" | 0' - 0 29/32" | 0' - 2 15/32" | 0' - 1 17/32" |
| WT6X126 | 0.26 SF | 126 | 1' - 1" | 0' - 7 23/32" | 0' - 3 1/8" | 0' - 0 7/8" | 0' - 2 1/4" | 0' - 1 13/32" |
| WT6X115 | 0.24 SF | 115 | 1' - 0 29/32" | 0' - 7 17/32" | 0' - 2 15/16" | 0' - 0 7/8" | 0' - 2 1/16" | 0' - 1 9/32" |
| WT6X105 | 0.21 SF | 105 | 1' - 0 13/16" | 0' - 7 3/8" | 0' - 2 13/16" | 0' - 0 29/32" | 0' - 1 29/32" | 0' - 1 3/16" |
| WT6X95 | 0.19 SF | 95 | 1' - 0 11/16" | 0' - 7 3/16" | 0' - 2 5/8" | 0' - 0 7/8" | 0' - 1 3/4" | 0' - 1 1/16" |
| WT6X85 | 0.17 SF | 85 | 1' - 0 19/32" | 0' - 7 1/32" | 0' - 2 7/16" | 0' - 0 7/8" | 0' - 1 9/16" | 0' - 0 31/32" |
| WT6X76 | 0.16 SF | 76 | 1' - 0 1/2" | 0' - 6 7/8" | 0' - 2 5/16" | 0' - 0 29/32" | 0' - 1 13/32" | 0' - 0 7/8" |
| WT6X68 | 0.14 SF | 68 | 1' - 0 13/32" | 0' - 6 23/32" | 0' - 2 1/8" | 0' - 0 7/8" | 0' - 1 1/4" | 0' - 0 25/32" |
| WT6X60 | 0.12 SF | 60 | 1' - 0 5/16" | 0' - 6 9/16" | 0' - 2" | 0' - 0 7/8" | 0' - 1 1/8" | 0' - 0 23/32" |
| WT6X53 | 0.11 SF | 53 | 1' - 0 3/16" | 0' - 6 7/16" | 0' - 1 7/8" | 0' - 0 7/8" | 0' - 1" | 0' - 0 5/8" |
| WT6X48 | 0.1 SF | 48 | 1' - 0 3/16" | 0' - 6 3/8" | 0' - 1 13/16" | 0' - 0 29/32" | 0' - 0 29/32" | 0' - 0 9/16" |
| WT6X43.5 | 0.09 SF | 43.5 | 1' - 0 3/32" | 0' - 6 9/32" | 0' - 1 11/16" | 0' - 0 7/8" | 0' - 0 13/16" | 0' - 0 1/2" |
| WT6X39.5 | 0.08 SF | 39.5 | 1' - 0 3/32" | 0' - 6 3/16" | 0' - 1 5/8" | 0' - 0 7/8" | 0' - 0 3/4" | 0' - 0 15/32" |
| WT6X36 | 0.07 SF | 36 | 1' - 0" | 0' - 6 1/8" | 0' - 1 9/16" | 0' - 0 29/32" | 0' - 0 21/32" | 0' - 0 7/16" |
| WT6X32.5 | 0.07 SF | 32.5 | 1' - 0" | 0' - 6 1/16" | 0' - 1 1/2" | 0' - 0 29/32" | 0' - 0 19/32" | 0' - 0 3/8" |
| WT6X29 | 0.06 SF | 29 | 0' - 10" | 0' - 6 3/32" | 0' - 1 1/2" | 0' - 0 7/8" | 0' - 0 5/8" | 0' - 0 3/8" |
| WT6X26.5 | 0.05 SF | 26.5 | 0' - 10" | 0' - 6 1/32" | 0' - 1 3/8" | 0' - 0 13/16" | 0' - 0 9/16" | 0' - 0 11/32" |
| WT6X25 | 0.05 SF | 25 | 0' - 8 3/32" | 0' - 6 3/32" | 0' - 1 1/2" | 0' - 0 7/8" | 0' - 0 5/8" | 0' - 0 3/8" |
| WT6X22.5 | 0.05 SF | 22.5 | 0' - 8 1/16" | 0' - 6 1/32" | 0' - 1 3/8" | 0' - 0 13/16" | 0' - 0 9/16" | 0' - 0 11/32" |
| WT6X20 | 0.04 SF | 20 | 0' - 8" | 0' - 5 31/32" | 0' - 1 3/8" | 0' - 0 7/8" | 0' - 0 1/2" | 0' - 0 9/32" |
| WT6X17.5 | 0.04 SF | 17.5 | 0' - 6 9/16" | 0' - 6 1/4" | 0' - 1 3/16" | 0' - 0 21/32" | 0' - 0 17/32" | 0' - 0 5/16" |
| WT6X15 | 0.03 SF | 15 | 0' - 6 17/32" | 0' - 6 5/32" | 0' - 1 1/8" | 0' - 0 11/16" | 0' - 0 7/16" | 0' - 0 1/4" |
| WT6X13 | 0.03 SF | 13 | 0' - 6 1/2" | 0' - 6 1/8" | 0' - 1 1/16" | 0' - 0 11/16" | 0' - 0 3/8" | 0' - 0 7/32" |
| WT6X11 | 0.02 SF | 11 | 0' - 4 1/32" | 0' - 6 5/32" | 0' - 0 15/16" | 0' - 0 1/2" | 0' - 0 7/16" | 0' - 0 1/4" |
| WT6X9.5 | 0.02 SF | 9.5 | 0' - 4" | 0' - 6 3/32" | 0' - 0 7/8" | 0' - 0 17/32" | 0' - 0 11/32" | 0' - 0 1/4" |
| WT6X8 | 0.02 SF | 8 | 0' - 4" | 0' - 6" | 0' - 0 13/16" | 0' - 0 9/16" | 0' - 0 1/4" | 0' - 0 7/32" |
| WT6X7 | 0.01 SF | 7 | 0' - 3 31/32" | 0' - 5 31/32" | 0' - 0 3/4" | 0' - 0 17/32" | 0' - 0 7/32" | 0' - 0 3/16" |
| WT5X56 | 0.11 SF | 56 | 0' - 10 13/32" | 0' - 5 11/16" | 0' - 1 15/16" | 0' - 0 11/16" | 0' - 1 1/4" | 0' - 0 3/4" |
| WT5X50 | 0.1 SF | 50 | 0' - 10 5/16" | 0' - 5 9/16" | 0' - 1 13/16" | 0' - 0 11/16" | 0' - 1 1/8" | 0' - 0 11/16" |
| WT5X44 | 0.09 SF | 44 | 0' - 10 5/16" | 0' - 5 13/32" | 0' - 1 11/16" | 0' - 0 11/16" | 0' - 1" | 0' - 0 19/32" |
| WT5X38.5 | 0.08 SF | 38.5 | 0' - 10 3/16" | 0' - 5 5/16" | 0' - 1 9/16" | 0' - 0 11/16" | 0' - 0 7/8" | 0' - 0 17/32" |
| WT5X34 | 0.07 SF | 34 | 0' - 10 3/32" | 0' - 5 3/16" | 0' - 1 7/16" | 0' - 0 21/32" | 0' - 0 25/32" | 0' - 0 15/32" |
| WT5X30 | 0.06 SF | 30 | 0' - 10 3/32" | 0' - 5 1/8" | 0' - 1 3/8" | 0' - 0 11/16" | 0' - 0 11/16" | 0' - 0 13/32" |
| WT5X27 | 0.05 SF | 27 | 0' - 10" | 0' - 5 1/16" | 0' - 1 5/16" | 0' - 0 11/16" | 0' - 0 5/8" | 0' - 0 3/8" |
| WT5X24.5 | 0.05 SF | 24.5 | 0' - 10" | 0' - 5" | 0' - 1 1/4" | 0' - 0 11/16" | 0' - 0 9/16" | 0' - 0 11/32" |
| WT5X22.5 | 0.05 SF | 22.5 | 0' - 8 1/32" | 0' - 5 1/16" | 0' - 1 5/16" | 0' - 0 11/16" | 0' - 0 5/8" | 0' - 0 11/32" |
| WT5X19.5 | 0.04 SF | 19.5 | 0' - 8" | 0' - 4 31/32" | 0' - 1 3/16" | 0' - 0 21/32" | 0' - 0 17/32" | 0' - 0 5/16" |
| WT5X16.5 | 0.03 SF | 16.5 | 0' - 7 31/32" | 0' - 4 7/8" | 0' - 1 1/8" | 0' - 0 11/16" | 0' - 0 7/16" | 0' - 0 9/32" |
| WT5X15 | 0.03 SF | 15 | 0' - 5 13/16" | 0' - 5 1/4" | 0' - 1 1/8" | 0' - 0 5/8" | 0' - 0 1/2" | 0' - 0 5/16" |
| WT5X13 | 0.03 SF | 13 | 0' - 5 25/32" | 0' - 5 5/32" | 0' - 1 1/16" | 0' - 0 5/8" | 0' - 0 7/16" | 0' - 0 1/4" |
| WT5X11 | 0.02 SF | 11 | 0' - 5 3/4" | 0' - 5 3/32" | 0' - 0 15/16" | 0' - 0 9/16" | 0' - 0 3/8" | 0' - 0 1/4" |
| WT5X9.5 | 0.02 SF | 9.5 | 0' - 4 1/32" | 0' - 5 1/8" | 0' - 0 15/16" | 0' - 0 17/32" | 0' - 0 13/32" | 0' - 0 1/4" |
| WT5X8.5 | 0.02 SF | 8.5 | 0' - 4" | 0' - 5 1/16" | 0' - 0 7/8" | 0' - 0 17/32" | 0' - 0 11/32" | 0' - 0 1/4" |
| WT5X7.5 | 0.02 SF | 7.5 | 0' - 4" | 0' - 5" | 0' - 0 13/16" | 0' - 0 17/32" | 0' - 0 9/32" | 0' - 0 7/32" |
| WT5X6 | 0.01 SF | 6 | 0' - 3 31/32" | 0' - 4 15/16" | 0' - 0 3/4" | 0' - 0 17/32" | 0' - 0 7/32" | 0' - 0 3/16" |
| WT4X33.5 | 0.07 SF | 33.5 | 0' - 8 9/32" | 0' - 4 1/2" | 0' - 1 5/8" | 0' - 0 11/16" | 0' - 0 15/16" | 0' - 0 9/16" |
| WT4X29 | 0.06 SF | 29 | 0' - 8 7/32" | 0' - 4 3/8" | 0' - 1 1/2" | 0' - 0 11/16" | 0' - 0 13/16" | 0' - 0 1/2" |
| WT4X24 | 0.05 SF | 24 | 0' - 8 1/8" | 0' - 4 1/4" | 0' - 1 3/8" | 0' - 0 11/16" | 0' - 0 11/16" | 0' - 0 13/32" |
| WT4X20 | 0.04 SF | 20 | 0' - 8 1/16" | 0' - 4 1/8" | 0' - 1 1/4" | 0' - 0 11/16" | 0' - 0 9/16" | 0' - 0 3/8" |
| WT4X17.5 | 0.04 SF | 17.5 | 0' - 8 1/32" | 0' - 4 1/16" | 0' - 1 3/16" | 0' - 0 11/16" | 0' - 0 1/2" | 0' - 0 5/16" |
| WT4X15.5 | 0.03 SF | 15.5 | 0' - 8" | 0' - 4" | 0' - 1 1/8" | 0' - 0 11/16" | 0' - 0 7/16" | 0' - 0 9/32" |
| WT4X14 | 0.03 SF | 14 | 0' - 6 17/32" | 0' - 4 1/32" | 0' - 0 15/16" | 0' - 0 15/32" | 0' - 0 15/32" | 0' - 0 9/32" |
| WT4X12 | 0.02 SF | 12 | 0' - 6 1/2" | 0' - 3 31/32" | 0' - 0 7/8" | 0' - 0 15/32" | 0' - 0 13/32" | 0' - 0 1/4" |
| WT4X10.5 | 0.02 SF | 10.5 | 0' - 5 9/32" | 0' - 4 1/8" | 0' - 0 7/8" | 0' - 0 15/32" | 0' - 0 13/32" | 0' - 0 1/4" |
| WT4X9 | 0.02 SF | 9 | 0' - 5 1/4" | 0' - 4 1/16" | 0' - 0 13/16" | 0' - 0 15/32" | 0' - 0 11/32" | 0' - 0 7/32" |
| WT4X7.5 | 0.02 SF | 7.5 | 0' - 4 1/32" | 0' - 4 1/16" | 0' - 0 13/16" | 0' - 0 1/2" | 0' - 0 5/16" | 0' - 0 1/4" |
| WT4X6.5 | 0.01 SF | 6.5 | 0' - 4" | 0' - 4" | 0' - 0 3/4" | 0' - 0 1/2" | 0' - 0 1/4" | 0' - 0 7/32" |
| WT4X5 | 0.01 SF | 5 | 0' - 3 15/16" | 0' - 3 15/16" | 0' - 0 11/16" | 0' - 0 15/32" | 0' - 0 7/32" | 0' - 0 5/32" |
| WT3X12.5 | 0.03 SF | 12.5 | 0' - 6 3/32" | 0' - 3 3/16" | 0' - 0 15/16" | 0' - 0 15/32" | 0' - 0 15/32" | 0' - 0 5/16" |
| WT3X10 | 0.02 SF | 10 | 0' - 6 1/32" | 0' - 3 3/32" | 0' - 0 7/8" | 0' - 0 1/2" | 0' - 0 3/8" | 0' - 0 1/4" |
| WT3X7.5 | 0.02 SF | 7.5 | 0' - 6" | 0' - 3" | 0' - 0 3/4" | 0' - 0 1/2" | 0' - 0 1/4" | 0' - 0 7/32" |
| WT3X8 | 0.02 SF | 8 | 0' - 4 1/32" | 0' - 3 1/8" | 0' - 0 7/8" | 0' - 0 15/32" | 0' - 0 13/32" | 0' - 0 1/4" |
| WT3X6 | 0.01 SF | 6 | 0' - 4" | 0' - 3 1/32" | 0' - 0 3/4" | 0' - 0 15/32" | 0' - 0 9/32" | 0' - 0 7/32" |
| WT3X4.5 | 0.01 SF | 4.5 | 0' - 3 15/16" | 0' - 2 15/16" | 0' - 0 11/16" | 0' - 0 15/32" | 0' - 0 7/32" | 0' - 0 5/32" |
| WT3X4.25 | 0.01 SF | 4.25 | 0' - 3 15/16" | 0' - 2 29/32" | 0' - 0 11/16" | 0' - 0 1/2" | 0' - 0 3/16" | 0' - 0 5/32" |
| WT2.5X9.5 | 0.02 SF | 9.5 | 0' - 5 1/32" | 0' - 2 19/32" | 0' - 0 13/16" | 0' - 0 3/8" | 0' - 0 7/16" | 0' - 0 9/32" |
| WT2.5X8 | 0.02 SF | 8 | 0' - 5" | 0' - 2 1/2" | 0' - 0 3/4" | 0' - 0 3/8" | 0' - 0 3/8" | 0' - 0 1/4" |
| WT2X6.5 | 0.01 SF | 6.5 | 0' - 4 1/16" | 0' - 2 3/32" | 0' - 0 3/4" | 0' - 0 13/32" | 0' - 0 11/32" | 0' - 0 9/32" |
